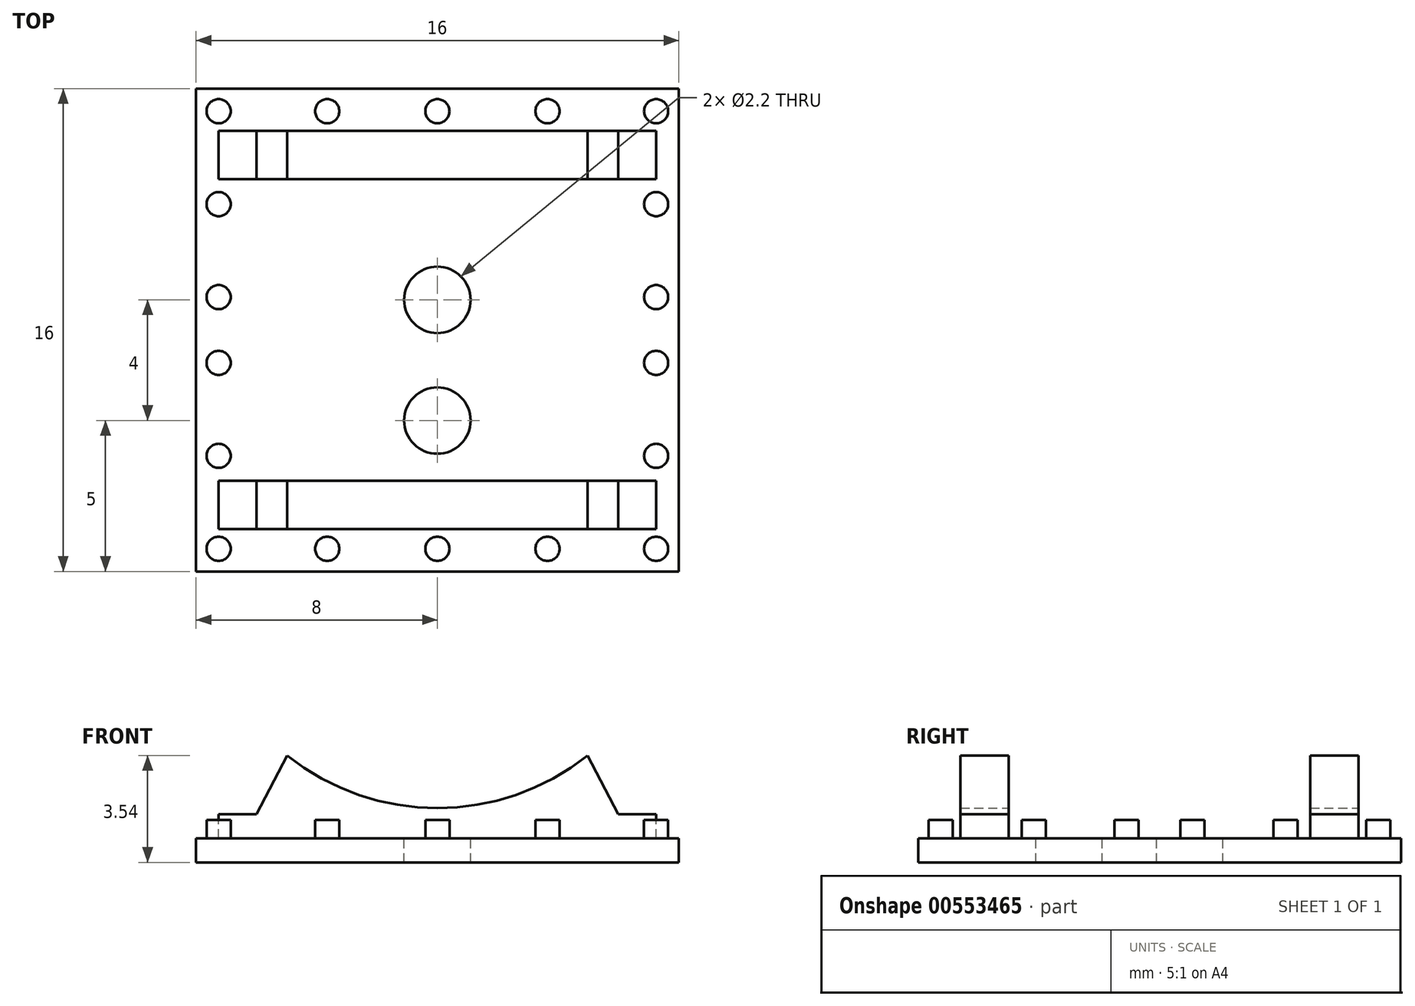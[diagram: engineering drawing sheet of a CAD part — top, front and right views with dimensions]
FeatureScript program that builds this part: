
annotation { "Feature Type Name" : "Feature", "Feature Type Description" : "" }
export const myFeature = defineFeature(function(context is Context, id is Id, definition is map)
    precondition{}
    {
        {
            var Q0;
            Q0=qCreatedBy(makeId("Top.planeOp"),FACE);
            var sketch = newSketch(context, id + "F0", { "sketchPlane" : qUnion([Q0])});
            skLineSegment(sketch, "E0.bottom", {"start": v(-8, -8) * mm, "end": v(8, -8) * mm});
            skLineSegment(sketch, "E0.top", {"start": v(-8, 8) * mm, "end": v(8, 8) * mm});
            skLineSegment(sketch, "E0.left", {"start": v(-8, -8) * mm, "end": v(-8, 8) * mm});
            skLineSegment(sketch, "E0.right", {"start": v(8, -8) * mm, "end": v(8, 8) * mm});
            skPoint(sketch, "E0.middle", {"position": v(0, 0) * mm});
            skSolve(sketch);
        }
        {
            var Q0;
            Q0 = qSketchRegion(id + "F0", true);
            extrude(context, id + "F1", {"entities" : qUnion([Q0]), "depth" : 0.8 * mm, "offsetDistance" : 25 * mm});
        }
        {
            var Q0;
            Q0=makeQuery(id+"F1.opExtrude","CAP_FACE",FACE,{"disambiguationData":[OSD([sQuery(id+"F0.wireOp",EDGE,"E0.bottom"),sQuery(id+"F0.wireOp",EDGE,"E0.top"),sQuery(id+"F0.wireOp",EDGE,"E0.left"),sQuery(id+"F0.wireOp",EDGE,"E0.right")])],"isStart":false});
            var sketch = newSketch(context, id + "F2", { "sketchPlane" : qUnion([Q0])});
            skLineSegment(sketch, "E1.bottom", {"start": v(-7.25, 7.25) * mm, "end": v(7.25, 7.25) * mm, "construction": true});
            skLineSegment(sketch, "E1.top", {"start": v(-7.25, -7.25) * mm, "end": v(7.25, -7.25) * mm, "construction": true});
            skLineSegment(sketch, "E1.left", {"start": v(-7.25, 7.25) * mm, "end": v(-7.25, -7.25) * mm, "construction": true});
            skLineSegment(sketch, "E1.right", {"start": v(7.25, 7.25) * mm, "end": v(7.25, -7.25) * mm, "construction": true});
            skPoint(sketch, "E1.middle", {"position": v(0, 0) * mm});
            skCircle(sketch, "E2", {"center": v(-7.25, 7.25) * mm, "radius": 0.4 * mm});
            skCircle(sketch, "E3", {"center": v(-7.25, 4.17) * mm, "radius": 0.4 * mm});
            skCircle(sketch, "E4", {"center": v(-7.25, 1.09) * mm, "radius": 0.4 * mm});
            skCircle(sketch, "E5", {"center": v(-7.25, -1.1) * mm, "radius": 0.4 * mm});
            skCircle(sketch, "E6", {"center": v(-7.25, -4.17) * mm, "radius": 0.4 * mm});
            skCircle(sketch, "E7", {"center": v(-7.25, -7.25) * mm, "radius": 0.4 * mm});
            skCircle(sketch, "E8", {"center": v(-3.65, 7.25) * mm, "radius": 0.4 * mm});
            skCircle(sketch, "E9", {"center": v(0, 7.25) * mm, "radius": 0.4 * mm});
            skCircle(sketch, "E10", {"center": v(3.65, 7.25) * mm, "radius": 0.4 * mm});
            skCircle(sketch, "E11", {"center": v(7.25, 7.25) * mm, "radius": 0.4 * mm});
            skCircle(sketch, "E12", {"center": v(7.25, 4.17) * mm, "radius": 0.4 * mm});
            skCircle(sketch, "E13", {"center": v(7.25, 1.1) * mm, "radius": 0.4 * mm});
            skCircle(sketch, "E14", {"center": v(7.25, -1.09) * mm, "radius": 0.4 * mm});
            skCircle(sketch, "E15", {"center": v(7.25, -4.17) * mm, "radius": 0.4 * mm});
            skCircle(sketch, "E16", {"center": v(7.25, -7.25) * mm, "radius": 0.4 * mm});
            skCircle(sketch, "E17", {"center": v(0, -7.25) * mm, "radius": 0.4 * mm});
            skCircle(sketch, "E18", {"center": v(3.65, -7.25) * mm, "radius": 0.4 * mm});
            skCircle(sketch, "E19", {"center": v(-3.65, -7.25) * mm, "radius": 0.4 * mm});
            skSolve(sketch);
        }
        {
            var Q0;
            Q0 = qSketchRegion(id + "F2", true);
            extrude(context, id + "F3", {"entities" : qUnion([Q0]), "operationType" : NewBodyOperationType.ADD, "depth" : 0.6 * mm, "offsetDistance" : 25 * mm});
        }
        {
            var Q0;
            Q0=qCreatedBy(makeId("Front.planeOp"),FACE);
            cPlane(context, id + "F4", {"entities" : qUnion([Q0]), "cplaneType" : CPlaneType.OFFSET, "offset" : 5 * mm, "width" : 150 * mm, "height" : 150 * mm});
        }
        {
            var Q0;
            Q0=qCreatedBy(id+"F4.planeOp",FACE);
            var sketch = newSketch(context, id + "F5", { "sketchPlane" : qUnion([Q0])});
            skArc(sketch, "E20", {"start": v(-4.5, 4.44) * mm, "mid": v(0, 2.8) * mm, "end": v(4.5, 4.44) * mm});
            skLineSegment(sketch, "E21.0", {"start": v(-8, 0.8) * mm, "end": v(8, 0.8) * mm, "construction": true});
            skLineSegment(sketch, "E22.bottom", {"start": v(-7.25, 0.8) * mm, "end": v(7.25, 0.8) * mm});
            skLineSegment(sketch, "E22.top", {"start": v(-7.25, 1.6) * mm, "end": v(-6, 1.6) * mm});
            skLineSegment(sketch, "E22.left", {"start": v(-7.25, 0.8) * mm, "end": v(-7.25, 1.6) * mm});
            skLineSegment(sketch, "E22.right", {"start": v(7.25, 0.8) * mm, "end": v(7.25, 1.6) * mm});
            skLineSegment(sketch, "E23", {"start": v(-6, 1.6) * mm, "end": v(-4.5, 4.44) * mm});
            skLineSegment(sketch, "E24", {"start": v(4.5, 4.44) * mm, "end": v(6, 1.6) * mm});
            skLineSegment(sketch, "E25.trimOffspring", {"start": v(6, 1.6) * mm, "end": v(7.25, 1.6) * mm});
            skSolve(sketch);
        }
        {
            var Q0;
            Q0 = qSketchRegion(id + "F5", true);
            extrude(context, id + "F6", {"entities" : qUnion([Q0]), "depth" : 1.6 * mm, "offsetDistance" : 25 * mm});
        }
        {
            var Q0;
            Q0=makeQuery(id+"F6.opExtrude","SWEPT_BODY",BODY,{"disambiguationData":[OSD([sQuery(id+"F5.wireOp",EDGE,"E20"),sQuery(id+"F5.wireOp",EDGE,"E22.bottom"),sQuery(id+"F5.wireOp",EDGE,"E22.top"),sQuery(id+"F5.wireOp",EDGE,"E22.left"),sQuery(id+"F5.wireOp",EDGE,"E22.right"),sQuery(id+"F5.wireOp",EDGE,"E23"),sQuery(id+"F5.wireOp",EDGE,"E24"),sQuery(id+"F5.wireOp",EDGE,"E25.trimOffspring")])]});
            var Q1;
            Q1=qCreatedBy(makeId("Front.planeOp"),FACE);
            mirror(context, id + "F7", {"operationType" : NewBodyOperationType.ADD, "entities" : qUnion([Q0]), "mirrorPlane" : qUnion([Q1])});
        }
        {
            var Q0;
            Q0=qCreatedBy(id+"F4.planeOp",FACE);
            var sketch = newSketch(context, id + "F8", { "sketchPlane" : qUnion([Q0])});
            skArc(sketch, "E26.0", {"start": v(-4.5, 4.44) * mm, "mid": v(0, 2.8) * mm, "end": v(4.5, 4.44) * mm, "construction": true});
            skCircle(sketch, "E27", {"center": v(0, 9.8) * mm, "radius": 8 * mm});
            skSolve(sketch);
        }
        {
            var Q0;
            Q0 = qSketchRegion(id + "F8", true);
            extrude(context, id + "F9", {"entities" : qUnion([Q0]), "operationType" : NewBodyOperationType.REMOVE, "endBound" : BoundingType.SYMMETRIC, "depth" : 25 * mm, "offsetDistance" : 25 * mm});
        }
        {
            var Q0;
            Q0=makeQuery(id+"F1.opExtrude","CAP_FACE",FACE,{"disambiguationData":[OSD([sQuery(id+"F0.wireOp",EDGE,"E0.bottom"),sQuery(id+"F0.wireOp",EDGE,"E0.top"),sQuery(id+"F0.wireOp",EDGE,"E0.left"),sQuery(id+"F0.wireOp",EDGE,"E0.right")])],"isStart":false});
            var sketch = newSketch(context, id + "F10", { "sketchPlane" : qUnion([Q0])});
            skCircle(sketch, "E28", {"center": v(0, -3) * mm, "radius": 1.1 * mm});
            skCircle(sketch, "E29", {"center": v(0, 1) * mm, "radius": 1.1 * mm});
            skSolve(sketch);
        }
        {
            var Q0;
            Q0 = qSketchRegion(id + "F10", true);
            extrude(context, id + "F11", {"entities" : qUnion([Q0]), "operationType" : NewBodyOperationType.REMOVE, "endBound" : BoundingType.THROUGH_ALL, "oppositeDirection" : true, "depth" : 25 * mm, "offsetDistance" : 25 * mm});
        }
    });
